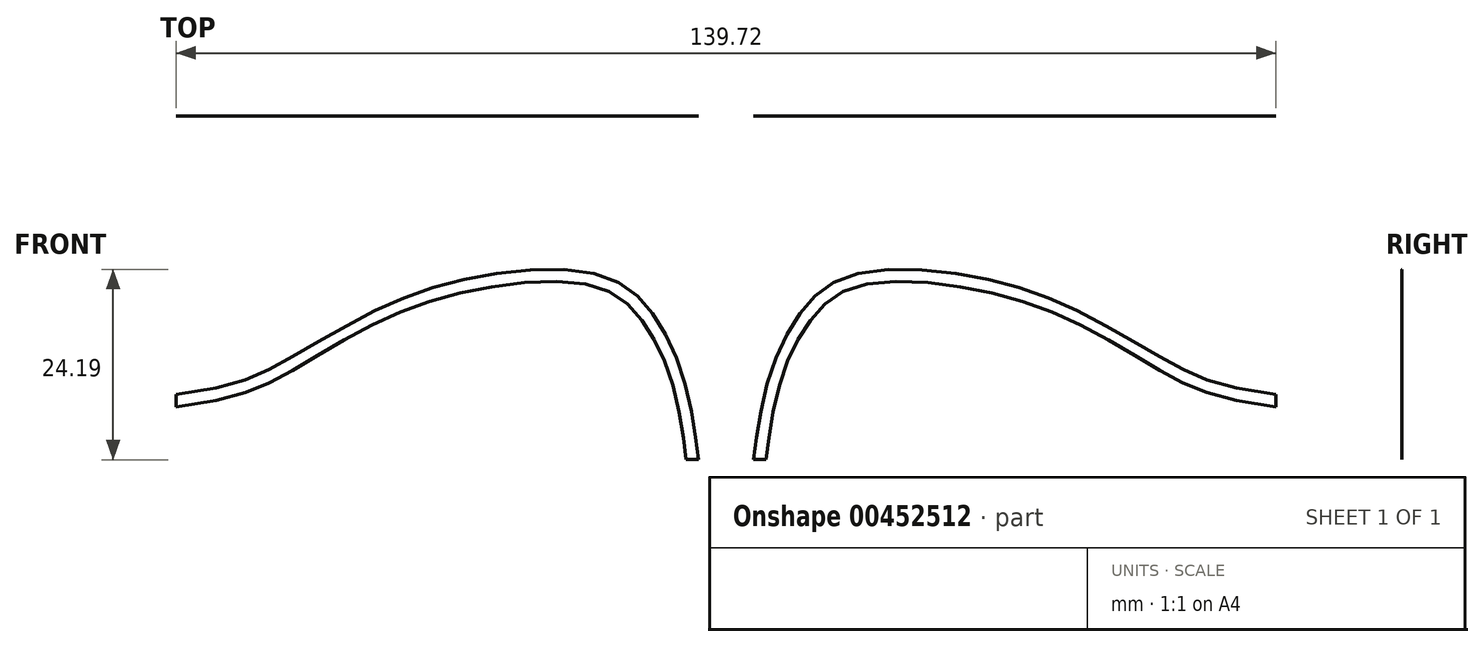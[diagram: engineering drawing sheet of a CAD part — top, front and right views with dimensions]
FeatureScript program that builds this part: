
annotation { "Feature Type Name" : "Feature", "Feature Type Description" : "" }
export const myFeature = defineFeature(function(context is Context, id is Id, definition is map)
    precondition{}
    {
        {
            var Q0;
            Q0=qCreatedBy(makeId("Front.planeOp"),FACE);
            var sketch = newSketch(context, id + "F0", { "sketchPlane" : qUnion([Q0])});
            skFitSpline(sketch, "E0", {"points": [v(-69.86, -4.03) * mm, v(-56.44, 0) * mm, v(-44.13, 6.83) * mm, v(-30.26, 11.18) * mm, v(-15.38, 10.96) * mm, v(-9.2, 6) * mm, v(-5.15, -2.92) * mm, v(-3.48, -12.32) * mm], "startDerivative": vector(137.1, 17.64) * mm, "endDerivative": vector(7.5, -55.33) * mm});
            skFitSpline(sketch, "E1", {"points": [v(-5.07, -12.32) * mm, v(-6.74, -2.92) * mm, v(-10.45, 5.03) * mm, v(-16.1, 9.54) * mm, v(-29.89, 9.63) * mm, v(-44.13, 5.24) * mm, v(-56.13, -1.56) * mm, v(-69.86, -5.62) * mm], "startDerivative": vector(-7.34, 52.58) * mm, "endDerivative": vector(-135.8, -17.17) * mm});
            skLineSegment(sketch, "E2", {"start": v(-69.86, -4.03) * mm, "end": v(-69.86, -5.62) * mm});
            skLineSegment(sketch, "E3", {"start": v(-5.07, -12.32) * mm, "end": v(-3.48, -12.32) * mm});
            skLineSegment(sketch, "E4.MirrorCS", {"start": v(69.86, -4.03) * mm, "end": v(69.86, -5.62) * mm});
            skLineSegment(sketch, "E5.MirrorCS", {"start": v(5.07, -12.32) * mm, "end": v(3.48, -12.32) * mm});
            skFitSpline(sketch, "E6.MirrorCS", {"points": [v(5.07, -12.32) * mm, v(6.74, -2.92) * mm, v(10.45, 5.03) * mm, v(16.1, 9.54) * mm, v(29.89, 9.63) * mm, v(44.13, 5.24) * mm, v(56.13, -1.56) * mm, v(69.86, -5.62) * mm], "startDerivative": vector(7.34, 52.58) * mm, "endDerivative": vector(135.8, -17.17) * mm});
            skFitSpline(sketch, "E7.MirrorCS", {"points": [v(69.86, -4.03) * mm, v(56.44, 0) * mm, v(44.13, 6.83) * mm, v(30.26, 11.18) * mm, v(15.38, 10.96) * mm, v(9.2, 6) * mm, v(5.15, -2.92) * mm, v(3.48, -12.32) * mm], "startDerivative": vector(-137.1, 17.64) * mm, "endDerivative": vector(-7.5, -55.33) * mm});
            skSolve(sketch);
        }
        {
            var Q0;
            Q0 = qSketchRegion(id + "F0", true);
            extrude(context, id + "F1", {"entities" : qUnion([Q0]), "depth" : 1 / 406.4 * mm, "offsetDistance" : 25.4 * mm});
        }
    });
